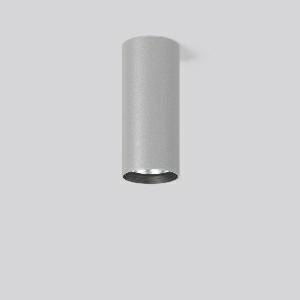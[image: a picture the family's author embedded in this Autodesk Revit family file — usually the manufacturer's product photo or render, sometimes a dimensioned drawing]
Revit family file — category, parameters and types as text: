
# Revit family: heledon_mini_a_931201_004_3_fe70
name_source: partatom
category: Lighting Fixtures
units: mm (PartAtom-declared; Revit-internal decimal feet)

## family parameters
Cut with Voids When Loaded = No
Host = Face
Light Source = No
Part Type = Normal
Room Calculation Point = No
Round Connector Dimension = Use Diameter
Shared = No

## types (1)
- HELEDON mini A (1 x LED Modul 935, 2500 lm, 3500)
    Apparent Load = 20 VA
    Approval mark = CE
    CIE Flux Codes = 99 100 100 100 100
    Color Rendering = 92
    Color Temperature = 3500
    Default Elevation = 1800 mm
    Description = Series: HELEDON mini
Cylindrical surface-mounted downlight. Housing: die-cast aluminium, powder-coated. Internal ceiling frame polycarbonate with bayonet mounting. Black plastic ring and recessed LED to prevent glare from the side. Optical assembly with reflector made of MIRO-Silver with 98% total light reflection for outstanding efficiency - can be changed without tools. Best colour rendering index Ra>90. Suitable for Ceiling mounting. Easy installation with a separate ceiling frame with bayonet mounting and plug connection. Driver integrated. Connected via plug-in connector. High quality converter without flickering and stroboscopic effect. The following accessories can be mounted without use of tools: interchangeable lenses, decorative glasses, honeycomb louvre, clear and frosted diffusers, white interchangeable plastic ring. 
Colour: silver
Diameter: 87 mm
Height: 197 mm
Lamp: LED
Socket: without socket
Colour temperature: 3500K
Colour rendering index (CRI): 92
System power: 20 W
Rated luminous flux: 2500 lm
Luminous efficiency: 125 lm/W
Control gear: Regulated power supply
Protection class: I
Type of protection: IP 20
    Height = 197 mm
    Lamp = 1 x LED Modul 935
    Lamp Light Flux = 2500 lm
    Lamp count = 1
    Length = 87 mm
    Lifetime = 50000 h
    Luminous efficacy = 125 lm/W
    Manufacturer = RZB
    ModVariant = No
    Model = 931201.004.3
    Mounting Place = Ceiling
    Mounting Type = Surface mounted
    Number of Poles = 1
    OnlyDefault = Yes
    Power Factor = 1
    Product Name = HELEDON mini A
    Product group = Surface mounted downlights
    ProductGroupID = 302
    Protection Class = Protection class I
    Protection Degree = IP 20
    RLX_Detail_Level = 1
    RLX_Emergency_Light_Flux = 0 lm
    RLX_Emergency_Type = 0
    RLX_Emergency_Type_DB = No
    RlxData = <blob elided: 108417 chars, md5=db144c77>
    Socket = socket
    Standby Power = 0 W
    System Light Flux = 2500 lm
    System Power = 20 W
    Type Comments = Product without accessories
    Type Image = 931188.004.jpg
    URL = http://relux.com
    VarID = ---
    Voltage = 230 V
    Voltage Range = 220-240 V
    Weight = 0.00 kg
    Width = 0 mm  [stored 0 ft]

note: [stored X ft] marks values corroborated as IEEE doubles in the binary element streams (Revit-internal decimal feet)

## geometry (parser evidence)
native form markers: Blend x4, Sweep x8
no freeform markers — native parametric forms only
